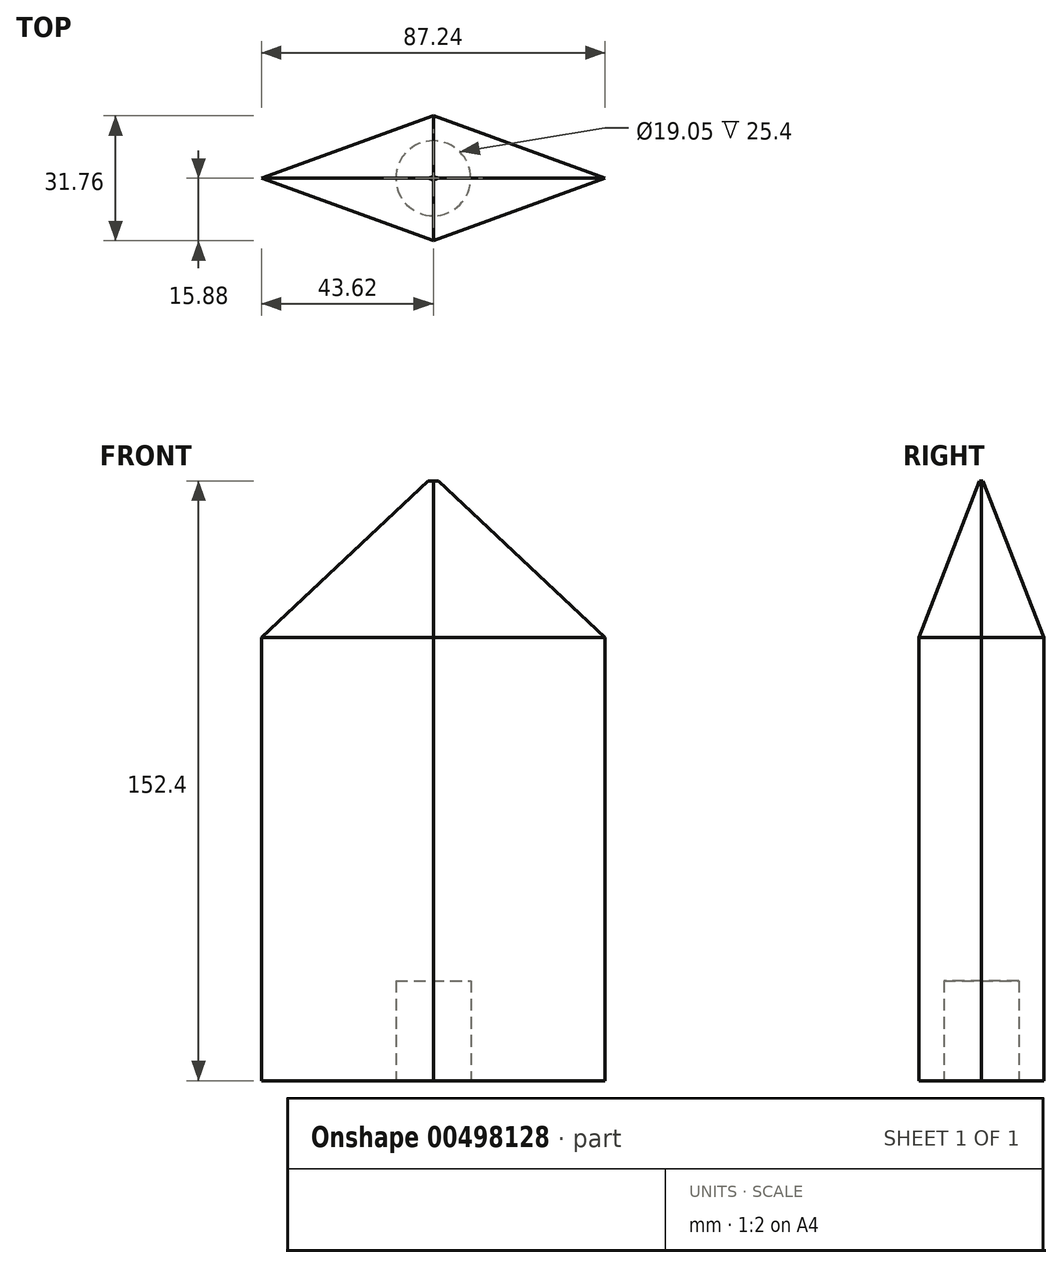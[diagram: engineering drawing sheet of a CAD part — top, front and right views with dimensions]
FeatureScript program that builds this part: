
annotation { "Feature Type Name" : "Feature", "Feature Type Description" : "" }
export const myFeature = defineFeature(function(context is Context, id is Id, definition is map)
    precondition{}
    {
        {
            var Q0;
            Q0=qCreatedBy(makeId("Top.planeOp"),FACE);
            var sketch = newSketch(context, id + "F0", { "sketchPlane" : qUnion([Q0])});
            skLineSegment(sketch, "E0.bottom", {"start": v(50.8, 15.88) * mm, "end": v(-50.8, 15.88) * mm});
            skLineSegment(sketch, "E0.top", {"start": v(50.8, -15.88) * mm, "end": v(-50.8, -15.88) * mm});
            skLineSegment(sketch, "E0.left", {"start": v(50.8, 15.88) * mm, "end": v(50.8, -15.88) * mm});
            skLineSegment(sketch, "E0.right", {"start": v(-50.8, 15.88) * mm, "end": v(-50.8, -15.88) * mm});
            skPoint(sketch, "E0.middle", {"position": v(0, 0) * mm});
            skSolve(sketch);
        }
        {
            var Q0;
            Q0=makeQuery(id+"F0.imprint","IMPRINT",FACE,{"disambiguationData":[TD([[makeQuery(id+"F0.imprint","IMPRINT",EDGE,{"derivedFrom":sQuery(id+"F0.wireOp",EDGE,"E0.bottom")}),1.0]])]});
            extrude(context, id + "F1", {"entities" : qUnion([Q0]), "depth" : 152.4 * mm, "offsetDistance" : 25.4 * mm});
        }
        {
            var Q0;
            Q0=makeQuery(id+"F1.opExtrude","SWEPT_EDGE",EDGE,{"disambiguationData":[OSD([sQuery(id+"F0.wireOp",EDGE,"E0.bottom"),sQuery(id+"F0.wireOp",EDGE,"E0.left")])]});
            var Q1;
            Q1=makeQuery(id+"F1.opExtrude","SWEPT_EDGE",EDGE,{"disambiguationData":[OSD([sQuery(id+"F0.wireOp",EDGE,"E0.top"),sQuery(id+"F0.wireOp",EDGE,"E0.left")])]});
            var Q2;
            Q2=makeQuery(id+"F1.opExtrude","SWEPT_EDGE",EDGE,{"disambiguationData":[OSD([sQuery(id+"F0.wireOp",EDGE,"E0.bottom"),sQuery(id+"F0.wireOp",EDGE,"E0.right")])]});
            var Q3;
            Q3=makeQuery(id+"F1.opExtrude","SWEPT_EDGE",EDGE,{"disambiguationData":[OSD([sQuery(id+"F0.wireOp",EDGE,"E0.top"),sQuery(id+"F0.wireOp",EDGE,"E0.right")])]});
            chamfer(context, id + "F2", {"entities" : qUnion([Q0, Q1, Q2, Q3]), "chamferType" : ChamferType.OFFSET_ANGLE, "width" : 50.8 * mm, "oppositeDirection" : false, "angle" : 20 * degree, "tangentPropagation" : true});
        }
        {
            var Q0;
            Q0=makeQuery(id+"F1.opExtrude","CAP_FACE",FACE,{"disambiguationData":[OSD([sQuery(id+"F0.wireOp",EDGE,"E0.bottom"),sQuery(id+"F0.wireOp",EDGE,"E0.top"),sQuery(id+"F0.wireOp",EDGE,"E0.left"),sQuery(id+"F0.wireOp",EDGE,"E0.right")])],"isStart":true});
            var sketch = newSketch(context, id + "F3", { "sketchPlane" : qUnion([Q0])});
            skCircle(sketch, "E1", {"center": v(0, 0) * mm, "radius": 9.53 * mm});
            skSolve(sketch);
        }
        {
            var Q0;
            Q0 = qSketchRegion(id + "F3", true);
            extrude(context, id + "F4", {"entities" : qUnion([Q0]), "operationType" : NewBodyOperationType.REMOVE, "oppositeDirection" : true, "depth" : 25.4 * mm, "offsetDistance" : 25.4 * mm});
        }
        {
            var Q0;
            {var subQ0=sQuery(id+"F0.wireOp",EDGE,"E0.right");var subQ1=sQuery(id+"F0.wireOp",EDGE,"E0.bottom");Q0=makeQuery(id+"F2.opChamfer","BLEND_EDGE",EDGE,{"blendedFrom":[makeQuery(id+"F1.opExtrude","SWEPT_EDGE",EDGE,{"disambiguationData":[OSD([subQ1,subQ0])]}),makeQuery(id+"F1.opExtrude","CAP_FACE",FACE,{"disambiguationData":[OSD([subQ1,sQuery(id+"F0.wireOp",EDGE,"E0.top"),sQuery(id+"F0.wireOp",EDGE,"E0.left"),subQ0])],"isStart":false})],"blendedInto":[makeQuery(id+"F1.opExtrude","CAP_FACE",FACE,{"disambiguationData":[OSD([subQ1,sQuery(id+"F0.wireOp",EDGE,"E0.top"),sQuery(id+"F0.wireOp",EDGE,"E0.left"),subQ0])],"isStart":false})]});}
            var Q1;
            {var subQ0=sQuery(id+"F0.wireOp",EDGE,"E0.right");var subQ1=sQuery(id+"F0.wireOp",EDGE,"E0.top");Q1=makeQuery(id+"F2.opChamfer","BLEND_EDGE",EDGE,{"blendedFrom":[makeQuery(id+"F1.opExtrude","SWEPT_EDGE",EDGE,{"disambiguationData":[OSD([subQ1,subQ0])]}),makeQuery(id+"F1.opExtrude","CAP_FACE",FACE,{"disambiguationData":[OSD([sQuery(id+"F0.wireOp",EDGE,"E0.bottom"),subQ1,sQuery(id+"F0.wireOp",EDGE,"E0.left"),subQ0])],"isStart":false})],"blendedInto":[makeQuery(id+"F1.opExtrude","CAP_FACE",FACE,{"disambiguationData":[OSD([sQuery(id+"F0.wireOp",EDGE,"E0.bottom"),subQ1,sQuery(id+"F0.wireOp",EDGE,"E0.left"),subQ0])],"isStart":false})]});}
            var Q2;
            {var subQ0=sQuery(id+"F0.wireOp",EDGE,"E0.left");var subQ1=sQuery(id+"F0.wireOp",EDGE,"E0.top");Q2=makeQuery(id+"F2.opChamfer","BLEND_EDGE",EDGE,{"blendedFrom":[makeQuery(id+"F1.opExtrude","SWEPT_EDGE",EDGE,{"disambiguationData":[OSD([subQ1,subQ0])]}),makeQuery(id+"F1.opExtrude","CAP_FACE",FACE,{"disambiguationData":[OSD([sQuery(id+"F0.wireOp",EDGE,"E0.bottom"),subQ1,subQ0,sQuery(id+"F0.wireOp",EDGE,"E0.right")])],"isStart":false})],"blendedInto":[makeQuery(id+"F1.opExtrude","CAP_FACE",FACE,{"disambiguationData":[OSD([sQuery(id+"F0.wireOp",EDGE,"E0.bottom"),subQ1,subQ0,sQuery(id+"F0.wireOp",EDGE,"E0.right")])],"isStart":false})]});}
            var Q3;
            {var subQ0=sQuery(id+"F0.wireOp",EDGE,"E0.left");var subQ1=sQuery(id+"F0.wireOp",EDGE,"E0.bottom");Q3=makeQuery(id+"F2.opChamfer","BLEND_EDGE",EDGE,{"blendedFrom":[makeQuery(id+"F1.opExtrude","SWEPT_EDGE",EDGE,{"disambiguationData":[OSD([subQ1,subQ0])]}),makeQuery(id+"F1.opExtrude","CAP_FACE",FACE,{"disambiguationData":[OSD([subQ1,sQuery(id+"F0.wireOp",EDGE,"E0.top"),subQ0,sQuery(id+"F0.wireOp",EDGE,"E0.right")])],"isStart":false})],"blendedInto":[makeQuery(id+"F1.opExtrude","CAP_FACE",FACE,{"disambiguationData":[OSD([subQ1,sQuery(id+"F0.wireOp",EDGE,"E0.top"),subQ0,sQuery(id+"F0.wireOp",EDGE,"E0.right")])],"isStart":false})]});}
            chamfer(context, id + "F5", {"entities" : qUnion([Q0, Q1, Q2, Q3]), "chamferType" : ChamferType.OFFSET_ANGLE, "width" : 14.48 * mm, "oppositeDirection" : false, "angle" : 70 * degree, "tangentPropagation" : true});
        }
    });
